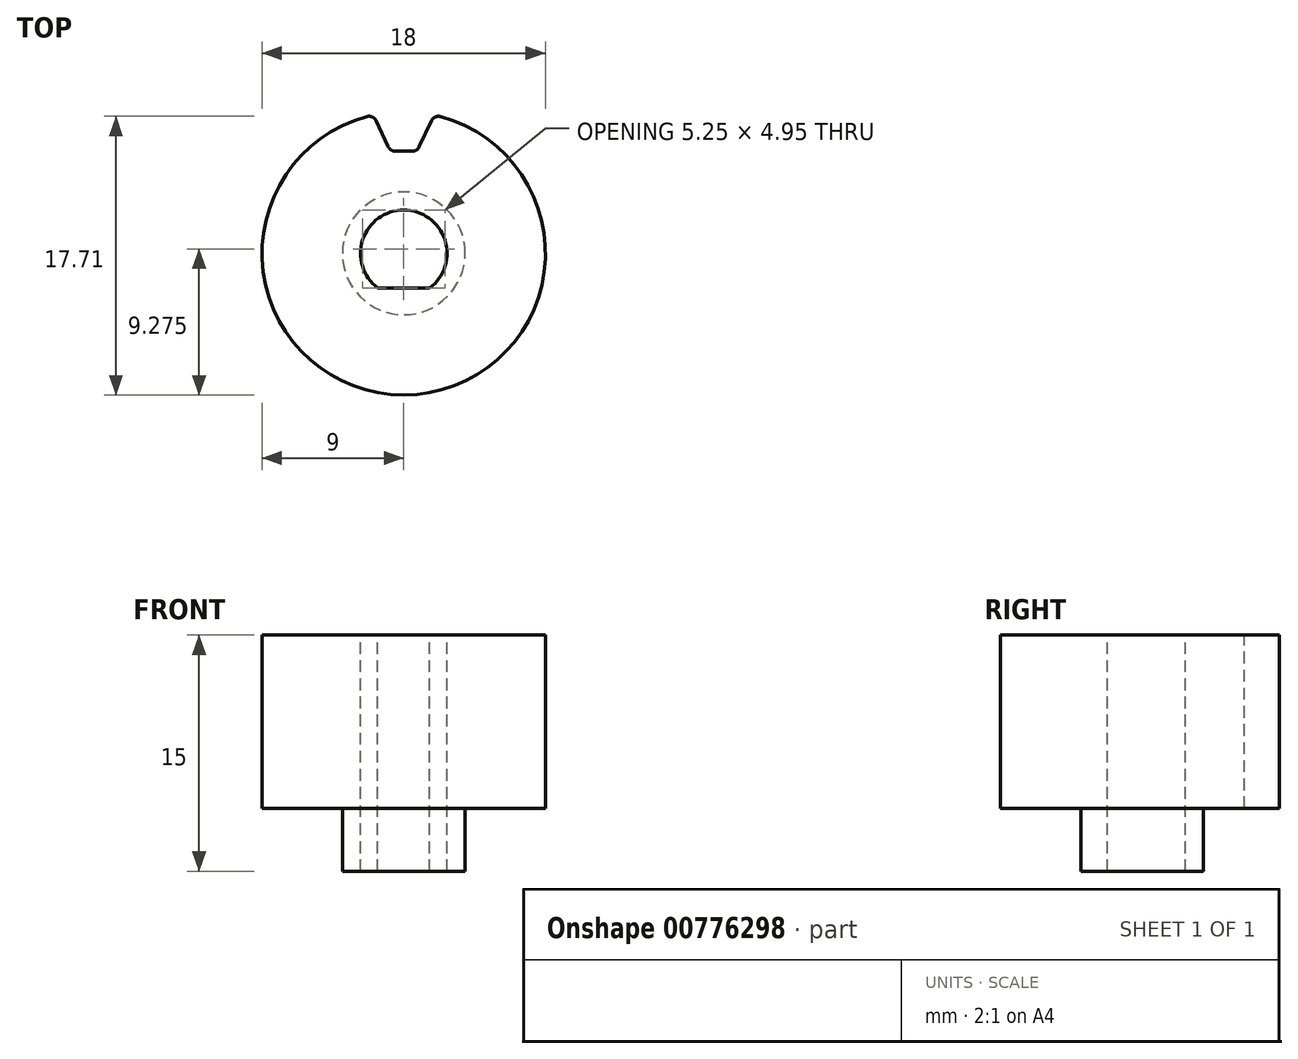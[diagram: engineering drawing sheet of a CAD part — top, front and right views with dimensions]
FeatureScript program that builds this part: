
annotation { "Feature Type Name" : "Feature", "Feature Type Description" : "" }
export const myFeature = defineFeature(function(context is Context, id is Id, definition is map)
    precondition{}
    {
        {
            var Q0;
            Q0=qCreatedBy(makeId("Front.planeOp"),FACE);
            var sketch = newSketch(context, id + "F0", { "sketchPlane" : qUnion([Q0])});
            skLineSegment(sketch, "E0.bottom", {"start": v(0, 0) * mm, "end": v(-9, 0) * mm});
            skLineSegment(sketch, "E0.top", {"start": v(0, 11) * mm, "end": v(-9, 11) * mm});
            skLineSegment(sketch, "E0.left", {"start": v(0, 0) * mm, "end": v(0, 11) * mm});
            skLineSegment(sketch, "E0.right", {"start": v(-9, 0) * mm, "end": v(-9, 11) * mm});
            skLineSegment(sketch, "E1", {"start": v(0, 13.09) * mm, "end": v(0, -1.72) * mm, "construction": true});
            skSolve(sketch);
        }
        {
            var Q0;
            Q0 = qSketchRegion(id + "F0", true);
            var Q1;
            Q1=sQuery(id+"F0.wireOp",EDGE,"E0.left");
            revolve(context, id + "F1", {"surfaceOperationType" : NewSurfaceOperationType.NEW, "entities" : qUnion([Q0]), "axis" : qUnion([Q1]), "revolveType" : RevolveType.FULL});
        }
        {
            var Q0;
            Q0=makeQuery(id+"F1.opRevolve","SWEPT_FACE",FACE,{"disambiguationData":[OSD([sQuery(id+"F0.wireOp",EDGE,"E0.top")])]});
            var sketch = newSketch(context, id + "F2", { "sketchPlane" : qUnion([Q0])});
            skArc(sketch, "E2", {"start": v(0.5, 6.48) * mm, "mid": v(0, 6.5) * mm, "end": v(-0.5, 6.48) * mm});
            skLineSegment(sketch, "E3", {"start": v(0, -7.74) * mm, "end": v(0, 8.38) * mm, "construction": true});
            skLineSegment(sketch, "E4", {"start": v(1.76, 8.42) * mm, "end": v(0.99, 6.77) * mm});
            skPoint(sketch, "E5", {"position": v(0, 9) * mm});
            skPoint(sketch, "E6", {"position": v(0, 6.5) * mm});
            skLineSegment(sketch, "E7.MirrorCS", {"start": v(-1.76, 8.42) * mm, "end": v(-0.99, 6.77) * mm});
            skArc(sketch, "E8.0", {"start": v(-2.34, 8.7) * mm, "mid": v(0, -9) * mm, "end": v(2.34, 8.7) * mm});
            skPoint(sketch, "E9.visualSharp", {"position": v(-1.93, 8.8) * mm});
            skArc(sketch, "E9.filletArc", {"start": v(-1.76, 8.42) * mm, "mid": v(-2, 8.66) * mm, "end": v(-2.34, 8.7) * mm});
            skPoint(sketch, "E10.visualSharp", {"position": v(1.93, 8.8) * mm});
            skArc(sketch, "E10.filletArc", {"start": v(2.34, 8.7) * mm, "mid": v(2, 8.66) * mm, "end": v(1.76, 8.42) * mm});
            skPoint(sketch, "E11.visualSharp", {"position": v(0.84, 6.45) * mm});
            skArc(sketch, "E11.filletArc", {"start": v(0.5, 6.48) * mm, "mid": v(0.79, 6.55) * mm, "end": v(0.99, 6.77) * mm});
            skPoint(sketch, "E12.visualSharp", {"position": v(-0.84, 6.45) * mm});
            skArc(sketch, "E12.filletArc", {"start": v(-0.99, 6.77) * mm, "mid": v(-0.79, 6.55) * mm, "end": v(-0.5, 6.48) * mm});
            skSolve(sketch);
        }
        {
            var Q0;
            Q0=makeQuery(id+"F2.imprint","IMPRINT",FACE,{"disambiguationData":[TD([[makeQuery(id+"F2.imprint","IMPRINT",EDGE,{"derivedFrom":sQuery(id+"F2.wireOp",EDGE,"E2")}),-1.0]])]});
            extrude(context, id + "F3", {"entities" : qUnion([Q0]), "operationType" : NewBodyOperationType.REMOVE, "oppositeDirection" : true, "depth" : 12 * mm, "offsetDistance" : 25 * mm});
        }
        {
            var Q0;
            Q0=makeQuery(id+"F1.opRevolve","SWEPT_FACE",FACE,{"disambiguationData":[OSD([sQuery(id+"F0.wireOp",EDGE,"E0.top")])]});
            var sketch = newSketch(context, id + "F4", { "sketchPlane" : qUnion([Q0])});
            skArc(sketch, "E13", {"start": v(1.65, -2.2) * mm, "mid": v(0, 2.75) * mm, "end": v(-1.65, -2.2) * mm});
            skLineSegment(sketch, "E14", {"start": v(-1.65, -2.2) * mm, "end": v(1.65, -2.2) * mm});
            skSolve(sketch);
        }
        {
            var Q0;
            Q0=makeQuery(id+"F4.imprint","IMPRINT",FACE,{"disambiguationData":[TD([[makeQuery(id+"F4.imprint","IMPRINT",EDGE,{"derivedFrom":sQuery(id+"F4.wireOp",EDGE,"E13")}),1.0]])]});
            extrude(context, id + "F5", {"entities" : qUnion([Q0]), "operationType" : NewBodyOperationType.REMOVE, "oppositeDirection" : true, "depth" : 25 * mm, "offsetDistance" : 25 * mm});
        }
        {
            var Q0;
            Q0=makeQuery(id+"F1.opRevolve","SWEPT_FACE",FACE,{"disambiguationData":[OSD([sQuery(id+"F0.wireOp",EDGE,"E0.bottom")])]});
            var sketch = newSketch(context, id + "F6", { "sketchPlane" : qUnion([Q0])});
            skArc(sketch, "E15.0", {"start": v(-4.21, -4.95) * mm, "mid": v(-3.82, -5.26) * mm, "end": v(-3.4, -5.53) * mm});
            skCircle(sketch, "E16", {"center": v(0, 0) * mm, "radius": 3.9 * mm});
            skSolve(sketch);
        }
        {
            var Q0;
            Q0=makeQuery(id+"F6.imprint","IMPRINT",FACE,{"disambiguationData":[TD([[makeQuery(id+"F6.imprint","IMPRINT",EDGE,{"derivedFrom":sQuery(id+"F6.wireOp",EDGE,"E16")}),1.0]])]});
            extrude(context, id + "F7", {"entities" : qUnion([Q0]), "operationType" : NewBodyOperationType.ADD, "depth" : 4 * mm, "offsetDistance" : 25 * mm});
        }
    });
